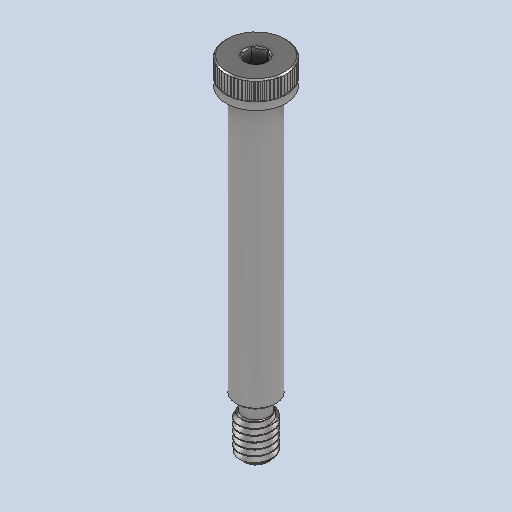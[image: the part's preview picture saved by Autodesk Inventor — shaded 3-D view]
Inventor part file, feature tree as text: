
AUTODESK INVENTOR PART (.ipt)
format: ipt  version: 2024 (Build 280153000, 153)  size: 450,560 bytes
history: native  units: in
note: dims shown in document units (in); Inventor stores cm internally (conversion verified against a paired STEP export)
features: chamfer x1
ambient origin geometry x8: Origin, YZ Plane, XZ Plane, XY Plane, X Axis, Y Axis, Z Axis, Center Point
bodies: Solid1 (feature_tree)
feature tree (1):
  chamfer  "Chamfer3"  [1 undecoded]
note: 1 required parameter value undecoded (feature->parameter linkage not recoverable at this tier; creation-order binding heuristic only, values carry confidence <= 0.55)
